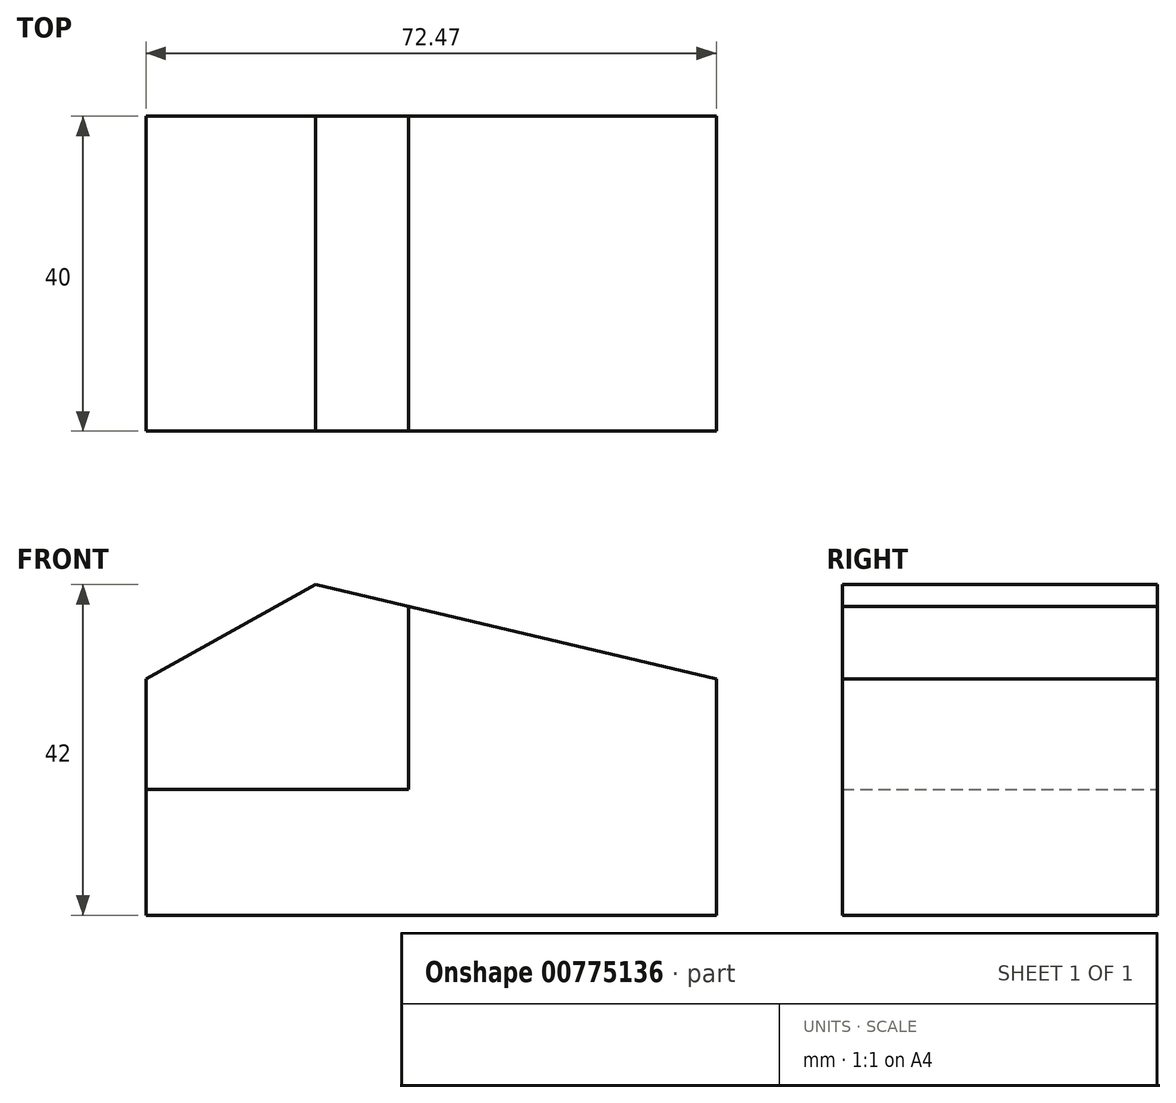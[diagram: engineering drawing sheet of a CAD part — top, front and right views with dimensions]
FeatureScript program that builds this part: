
annotation { "Feature Type Name" : "Feature", "Feature Type Description" : "" }
export const myFeature = defineFeature(function(context is Context, id is Id, definition is map)
    precondition{}
    {
        {
            var Q0;
            Q0=qCreatedBy(makeId("Front.planeOp"),FACE);
            var sketch = newSketch(context, id + "F0", { "sketchPlane" : qUnion([Q0])});
            skLineSegment(sketch, "E0", {"start": v(-36.51, 0) * mm, "end": v(-36.51, 30) * mm});
            skLineSegment(sketch, "E1", {"start": v(-36.51, 30) * mm, "end": v(-14.94, 42) * mm});
            skLineSegment(sketch, "E2", {"start": v(-14.94, 42) * mm, "end": v(35.96, 30) * mm});
            skLineSegment(sketch, "E3", {"start": v(35.96, 30) * mm, "end": v(35.96, 0) * mm});
            skLineSegment(sketch, "E4", {"start": v(-19.63, 28) * mm, "end": v(-19.63, 16) * mm});
            skLineSegment(sketch, "E5", {"start": v(-10.63, 28) * mm, "end": v(-10.63, 16) * mm});
            skLineSegment(sketch, "E6", {"start": v(-10.63, 16) * mm, "end": v(-19.63, 16) * mm});
            skLineSegment(sketch, "E7", {"start": v(-19.63, 28) * mm, "end": v(-10.63, 28) * mm});
            skLineSegment(sketch, "E8", {"start": v(-19.63, 16) * mm, "end": v(-36.51, 16) * mm});
            skPoint(sketch, "E8.endSnap0", {"position": v(-36.51, 15) * mm});
            skLineSegment(sketch, "E9", {"start": v(-10.63, 16) * mm, "end": v(-3.15, 16) * mm});
            skLineSegment(sketch, "E10", {"start": v(-3.15, 16) * mm, "end": v(-3.15, 39.22) * mm});
            skLineSegment(sketch, "E11", {"start": v(-3.15, 16) * mm, "end": v(-3.15, 0) * mm});
            skLineSegment(sketch, "E12", {"start": v(-3.15, 19.58) * mm, "end": v(30.07, 0) * mm});
            skLineSegment(sketch, "E13", {"start": v(-36.51, 0) * mm, "end": v(35.96, 0) * mm});
            skLineSegment(sketch, "E14", {"start": v(-14.94, 42) * mm, "end": v(-14.94, 0) * mm});
            skLineSegment(sketch, "E15", {"start": v(-36.51, 0) * mm, "end": v(-14.94, 0) * mm});
            skLineSegment(sketch, "E16", {"start": v(-14.94, 0) * mm, "end": v(35.96, 0) * mm});
            skSolve(sketch);
        }
        {
            var Q0;
            Q0=sQuery(id+"F0.wireOp",EDGE,"E13");
            var Q1;
            Q1=sQuery(id+"F0.wireOp",EDGE,"E0");
            var Q2;
            Q2=sQuery(id+"F0.wireOp",EDGE,"E1");
            var Q3;
            Q3=sQuery(id+"F0.wireOp",EDGE,"E2");
            var Q4;
            Q4=sQuery(id+"F0.wireOp",EDGE,"E3");
            extrude(context, id + "F1", {"bodyType" : ToolBodyType.SURFACE, "surfaceEntities" : qUnion([Q0, Q1, Q2, Q3, Q4]), "depth" : -40 * mm, "offsetDistance" : 25 * mm});
        }
        {
            var Q0;
            Q0=sQuery(id+"F0.wireOp",EDGE,"E8");
            var Q1;
            Q1=sQuery(id+"F0.wireOp",EDGE,"E6");
            var Q2;
            Q2=sQuery(id+"F0.wireOp",EDGE,"E9");
            var Q3;
            Q3=sQuery(id+"F0.wireOp",EDGE,"E10");
            extrude(context, id + "F2", {"bodyType" : ToolBodyType.SURFACE, "surfaceEntities" : qUnion([Q0, Q1, Q2, Q3]), "depth" : -40 * mm, "offsetDistance" : 25 * mm});
        }
    });
